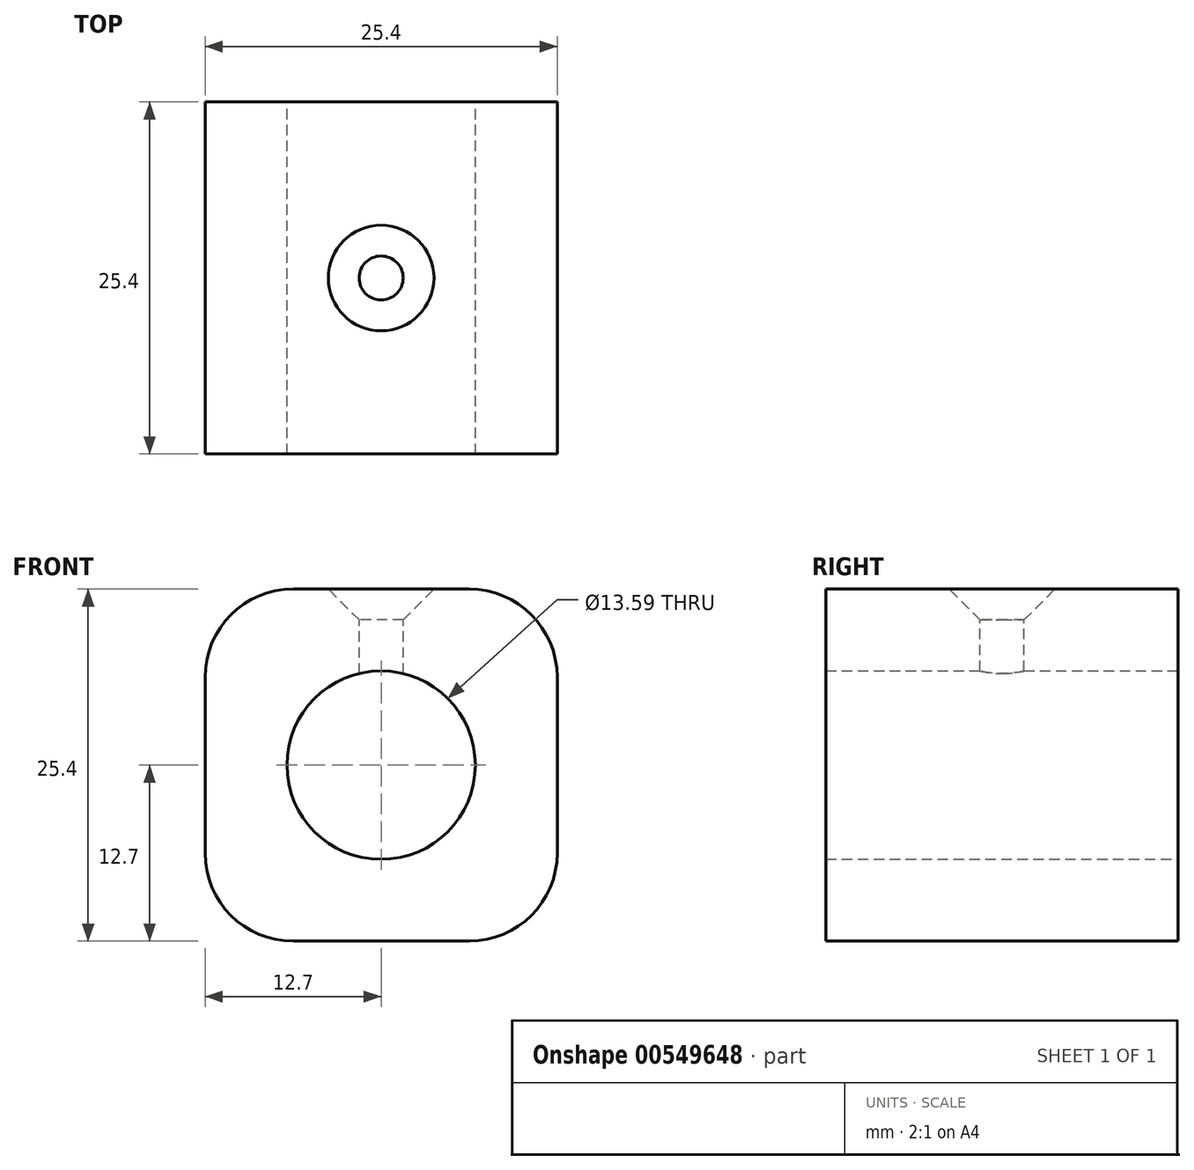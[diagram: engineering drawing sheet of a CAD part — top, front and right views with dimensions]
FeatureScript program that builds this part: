
annotation { "Feature Type Name" : "Feature", "Feature Type Description" : "" }
export const myFeature = defineFeature(function(context is Context, id is Id, definition is map)
    precondition{}
    {
        {
            var Q0;
            Q0=qCreatedBy(makeId("Front.planeOp"),FACE);
            var sketch = newSketch(context, id + "F0", { "sketchPlane" : qUnion([Q0])});
            skLineSegment(sketch, "E0.bottom", {"start": v(-12.7, -12.7) * mm, "end": v(12.7, -12.7) * mm});
            skLineSegment(sketch, "E0.top", {"start": v(-12.7, 12.7) * mm, "end": v(12.7, 12.7) * mm});
            skLineSegment(sketch, "E0.left", {"start": v(-12.7, -12.7) * mm, "end": v(-12.7, 12.7) * mm});
            skLineSegment(sketch, "E0.right", {"start": v(12.7, -12.7) * mm, "end": v(12.7, 12.7) * mm});
            skCircle(sketch, "E1", {"center": v(0, 0) * mm, "radius": 6.8 * mm});
            skCircle(sketch, "E2", {"center": v(0, 0) * mm, "radius": 3.12 * mm});
            skSolve(sketch);
        }
        {
            var Q0;
            Q0 = qSketchRegion(id + "F0", true);
            extrude(context, id + "F1", {"entities" : qUnion([Q0]), "endBound" : BoundingType.SYMMETRIC, "depth" : 25.4 * mm, "offsetDistance" : 25.4 * mm});
        }
        {
            var Q0;
            Q0=makeQuery(id+"F1.opExtrude","SWEPT_EDGE",EDGE,{"disambiguationData":[OSD([sQuery(id+"F0.wireOp",EDGE,"E0.top"),sQuery(id+"F0.wireOp",EDGE,"E0.right")])]});
            var Q1;
            Q1=makeQuery(id+"F1.opExtrude","SWEPT_EDGE",EDGE,{"disambiguationData":[OSD([sQuery(id+"F0.wireOp",EDGE,"E0.top"),sQuery(id+"F0.wireOp",EDGE,"E0.left")])]});
            var Q2;
            Q2=makeQuery(id+"F1.opExtrude","SWEPT_EDGE",EDGE,{"disambiguationData":[OSD([sQuery(id+"F0.wireOp",EDGE,"E0.bottom"),sQuery(id+"F0.wireOp",EDGE,"E0.left")])]});
            var Q3;
            Q3=makeQuery(id+"F1.opExtrude","SWEPT_EDGE",EDGE,{"disambiguationData":[OSD([sQuery(id+"F0.wireOp",EDGE,"E0.bottom"),sQuery(id+"F0.wireOp",EDGE,"E0.right")])]});
            fillet(context, id + "F2", {"entities" : qUnion([Q0, Q1, Q2, Q3]), "radius" : 6.35 * mm, "tangentPropagation" : true, "allowEdgeOverflow" : false});
        }
        {
            var Q0;
            Q0=makeQuery(id+"F1.opExtrude","SWEPT_FACE",FACE,{"disambiguationData":[OSD([sQuery(id+"F0.wireOp",EDGE,"E0.top")])]});
            var sketch = newSketch(context, id + "F3", { "sketchPlane" : qUnion([Q0])});
            skCircle(sketch, "E3", {"center": v(0, 0) * mm, "radius": 1.93 * mm});
            skPoint(sketch, "E3.centerSnap0", {"position": v(6.35, 0) * mm});
            skSolve(sketch);
        }
        {
            var Q0;
            Q0=sQuery(id+"F3.wireOp",VERTEX,"E3.center");
            var Q1;
            Q1=makeQuery(id+"F1.opExtrude","SWEPT_BODY",BODY,{"disambiguationData":[OSD([sQuery(id+"F0.wireOp",EDGE,"E0.bottom"),sQuery(id+"F0.wireOp",EDGE,"E0.top"),sQuery(id+"F0.wireOp",EDGE,"E0.left"),sQuery(id+"F0.wireOp",EDGE,"E0.right"),sQuery(id+"F0.wireOp",EDGE,"E1")])]});
            hole(context, id + "F4", {"style" : HoleStyle.C_SINK, "endStyle" : HoleEndStyle.BLIND, "holeDiameter" : 3.17 * mm, "cSinkDiameter" : 7.62 * mm, "cSinkAngle" : 90 * degree, "holeDepth" : 12.7 * mm, "isTappedThrough" : true, "tappedDepth" : 12.7 * mm, "tapClearance" : 3, "locations" : qUnion([Q0]), "scope" : qUnion([Q1])});
        }
    });
